# Revit family: AD-S6T - X Mount
name_source: partatom
category: Communication Devices
revit_build: Autodesk Revit 2014 (Build: 20130308_1515(x64)
units: mm (PartAtom-declared; Revit-internal decimal feet)

## types (1)
- AD-S6T - X Mount
    100V Taps = 60, 30, 15
    70V Taps = 60, 30, 15, 7.5
    Coverage Horizontal = 105.00°
    Coverage Vertical = 105.00°
    Default Elevation = 0 mm  [stored 0 ft]
    Depth = 215 mm
    Description = 6" 2-Way Small Format Surface Mount Loudspeaker
    Height = 365 mm  [stored 1.19751 ft]
    Impedance = 8
    Manufacturer = QSC Audio Products, LLC
    Manufacturer URL = www.qscaudio.com
    Model = AD-S6T
    Mount Box Depth = 25 mm  [stored 0.082021 ft]
    Mount Depth = 110 mm  [stored 0.360892 ft]
    Mount Height = 134 mm
    Mount Width = 110 mm  [stored 0.360892 ft]
    Power Handling = 150
    Product Documentation Link = http://www.qsc.com
    Product Page URL = http://www.qsc.com
    Regulatory Compliance = IP54
    SPL Max = 116
    Sensitivity = 89
    URL = http://www.qsc.com
    Weight Dimensional (kg) = 15.2
    Weight Dimensional (lb) = 33.4
    Weight Product (kg) = 6.2
    Weight Product (lb) = 13.6
    Width = 215 mm

note: [stored X ft] marks values corroborated as IEEE doubles in the binary element streams (Revit-internal decimal feet)

## geometry (parser evidence)
native form markers: Blend x2, Sweep x12
no freeform markers — native parametric forms only
